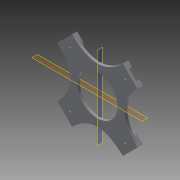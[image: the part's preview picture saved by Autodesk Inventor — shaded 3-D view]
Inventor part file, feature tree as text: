
AUTODESK INVENTOR PART (.ipt)
format: ipt  version: 2015 (Build 190159000, 159)  size: 252,416 bytes
history: native  units: mm
features: sketch x8, extrude x7, mirror x6, plane x2, projected_geometry x2, split x1, hole x1, chamfer x1
ambient origin geometry x8: Origin, YZ Plane, XZ Plane, XY Plane, X Axis, Y Axis, Z Axis, Center Point
bodies: Solid1 (feature_tree)
feature tree (28):
  extrude  "Extrusion1"  Depth=160.0mm
  split  "Split1"
  plane  "Work Plane1"
  plane  "Work Plane2"
  mirror  "Mirror1"
  mirror  "Mirror2"
  extrude  "Extrusion2"  TaperAngle=45.0deg  [1 undecoded]
  extrude  "Extrusion3"  Depth=10.0mm
  extrude  "Extrusion4"  Depth=6.0mm TaperAngle=0.0deg
  hole  "Hole1"  [1 undecoded]
  chamfer  "Chamfer1"  Distance=10.0mm
  mirror  "Mirror3"
  mirror  "Mirror4"
  extrude  "Extrusion5"  Depth=1.0mm TaperAngle=45.0deg
  mirror  "Mirror5"
  extrude  "Extrusion6"  Depth=10.0mm TaperAngle=0.0deg
  mirror  "Mirror6"
  extrude  "Extrusion7"  Depth=10.0mm TaperAngle=0.0deg
  sketch  "Sketch1"  dims[d0=160.0mm d1=160.0mm]
  sketch  "Sketch2"  dims[d2=5.0mm d3=0.0mm d4=45.0deg]
  projected_geometry  "Projected Loop1"
  sketch  "Sketch4"  dims[d5=29.5mm d6=10.0mm]
  sketch  "Sketch5"  dims[d7=6.0mm d8=0.0mm d9=6.0mm d10=0.0mm]
  projected_geometry  "Projected Loop2"
  sketch  "Sketch7"  dims[d11=10.0mm d12=3.0mm d13=0.0mm d14=10.0mm d15=10.0mm]
  sketch  "Sketch8"  dims[d16=4.0mm d17=6.0mm d18=4.0mm d19=2.0mm d20=90.0deg d21=8.0mm d22=20.594885mm d23=1.0mm d24=2.0mm d25=45.0deg]
  sketch  "Sketch9"  dims[d26=10.0mm d27=0.0mm d28=10.0mm d29=0.0mm]
  sketch  "Sketch10"  dims[d30=80.0mm d31=10.0mm d32=0.0mm]
note: 2 required parameter values undecoded (feature->parameter linkage not recoverable at this tier; creation-order binding heuristic only, values carry confidence <= 0.55)
